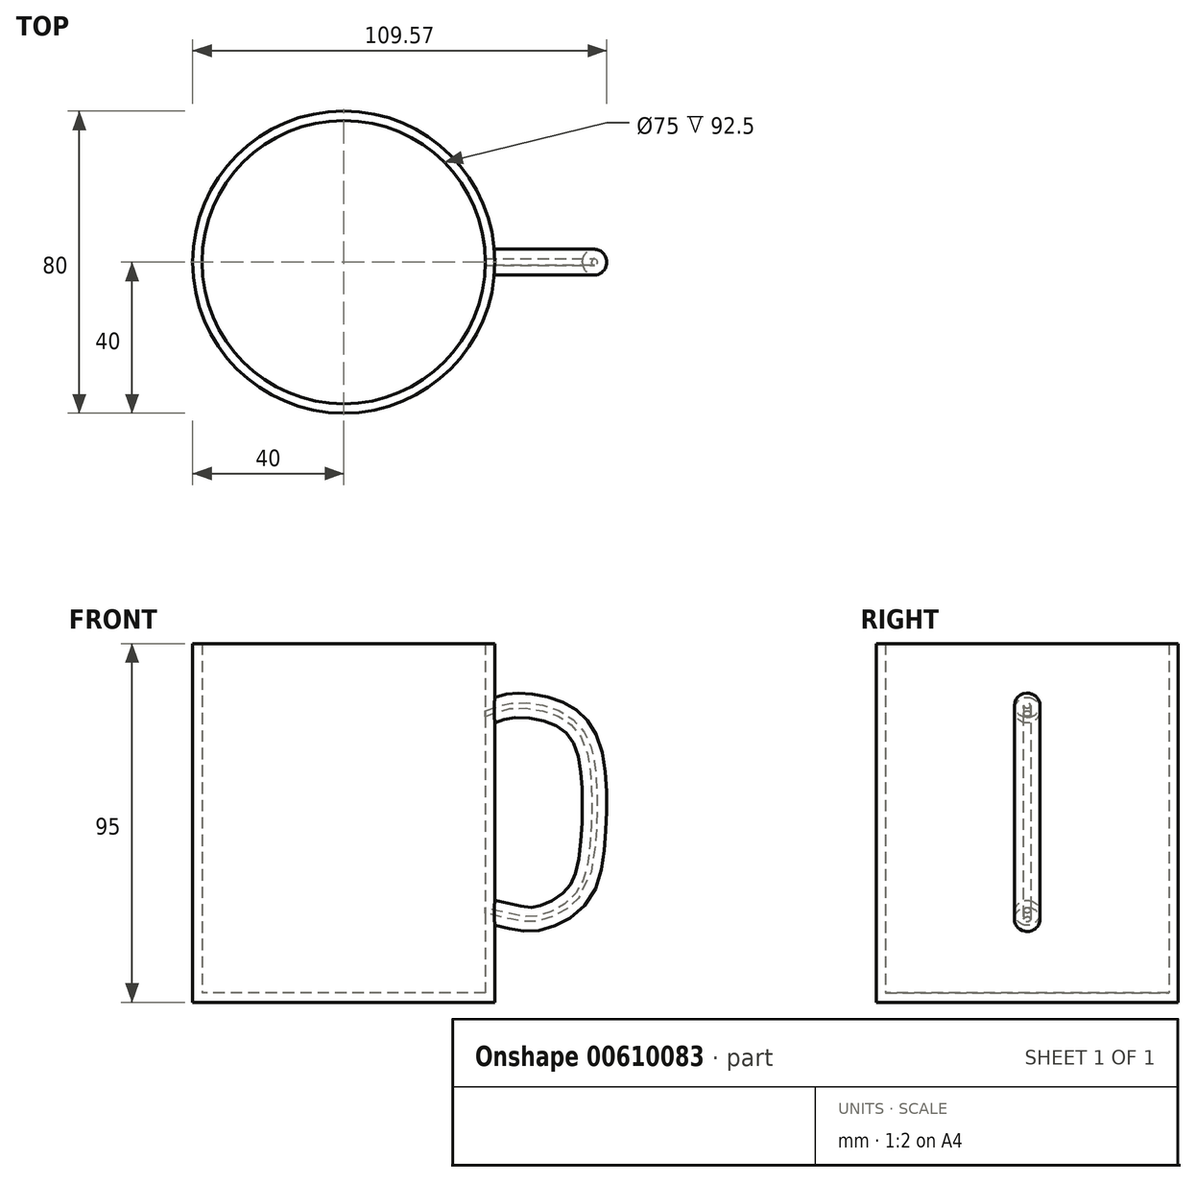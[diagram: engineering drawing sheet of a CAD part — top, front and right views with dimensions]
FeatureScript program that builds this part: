
annotation { "Feature Type Name" : "Feature", "Feature Type Description" : "" }
export const myFeature = defineFeature(function(context is Context, id is Id, definition is map)
    precondition{}
    {
        {
            var Q0;
            Q0=qCreatedBy(makeId("Top.planeOp"),FACE);
            var sketch = newSketch(context, id + "F0", { "sketchPlane" : qUnion([Q0])});
            skCircle(sketch, "E0", {"center": v(0, 0) * mm, "radius": 40 * mm});
            skSolve(sketch);
        }
        {
            var Q0;
            Q0 = qSketchRegion(id + "F0", true);
            extrude(context, id + "F1", {"entities" : qUnion([Q0]), "depth" : 95 * mm, "offsetDistance" : 25 * mm});
        }
        {
            var Q0;
            Q0=qCreatedBy(makeId("Right.planeOp"),FACE);
            cPlane(context, id + "F2", {"entities" : qUnion([Q0]), "cplaneType" : CPlaneType.OFFSET, "offset" : 40 * mm, "width" : 150 * mm, "height" : 150 * mm});
        }
        {
            var Q0;
            Q0=qCreatedBy(id+"F2.planeOp",FACE);
            var sketch = newSketch(context, id + "F3", { "sketchPlane" : qUnion([Q0])});
            skCircle(sketch, "E1", {"center": v(0, 77.37) * mm, "radius": 3.4 * mm});
            skSolve(sketch);
        }
        {
            var Q0;
            Q0=qCreatedBy(makeId("Front.planeOp"),FACE);
            var sketch = newSketch(context, id + "F4", { "sketchPlane" : qUnion([Q0])});
            skFitSpline(sketch, "E2", {"points": [v(39.18, 77.35) * mm, v(44.73, 78.79) * mm, v(55.42, 77.35) * mm, v(63.44, 70.97) * mm, v(66.32, 59.87) * mm, v(66.53, 47.94) * mm, v(64.68, 33.34) * mm, v(59.33, 25.53) * mm, v(50.49, 21.82) * mm, v(44.32, 22.44) * mm, v(36.95, 24.28) * mm], "startDerivative": vector(63.93, 23.45) * mm, "endDerivative": vector(-73.76, 24.48) * mm});
            skSolve(sketch);
        }
        {
            var Q0;
            Q0=makeQuery(id+"F3.imprint","IMPRINT",FACE,{"disambiguationData":[TD([[makeQuery(id+"F3.imprint","IMPRINT",EDGE,{"derivedFrom":sQuery(id+"F3.wireOp",EDGE,"E1")}),1.0]])]});
            var Q1;
            Q1=sQuery(id+"F4.wireOp",EDGE,"E2");
            sweep(context, id + "F5", {"operationType" : NewBodyOperationType.ADD, "profiles" : qUnion([Q0]), "path" : qUnion([Q1])});
        }
        {
            var Q0;
            Q0=makeQuery(id+"F1.opExtrude","CAP_FACE",FACE,{"disambiguationData":[OSD([sQuery(id+"F0.wireOp",EDGE,"E0")])],"isStart":false});
            shell(context, id + "F6", {"entities" : qUnion([Q0]), "thickness" : 2.5 * mm});
        }
    });
